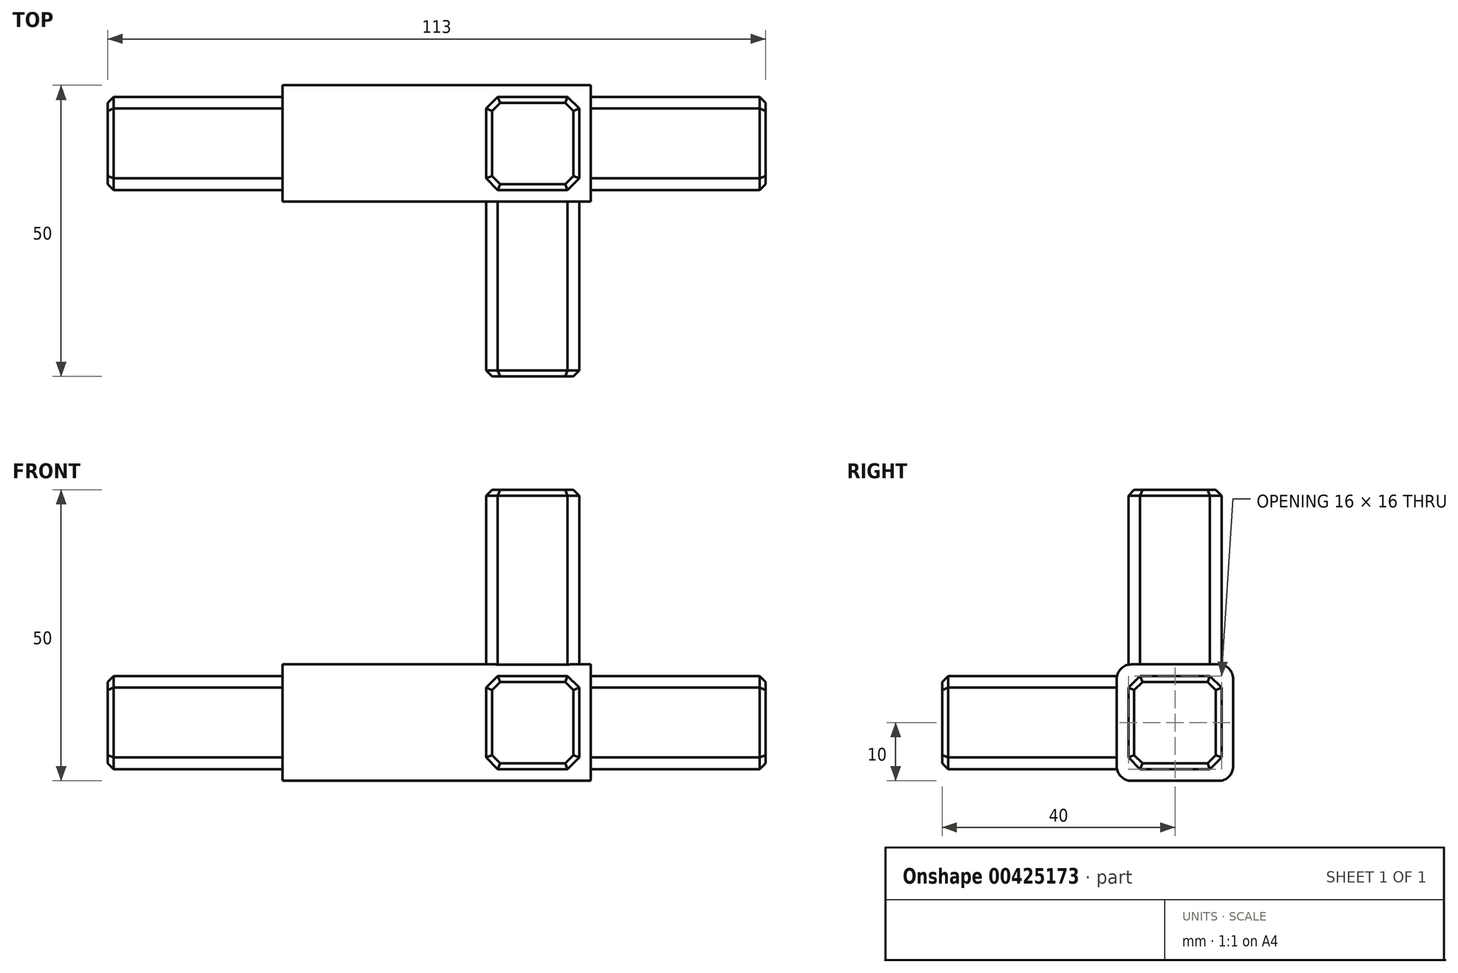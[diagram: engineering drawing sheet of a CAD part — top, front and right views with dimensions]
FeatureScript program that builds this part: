
annotation { "Feature Type Name" : "Feature", "Feature Type Description" : "" }
export const myFeature = defineFeature(function(context is Context, id is Id, definition is map)
    precondition{}
    {
        {
            var Q0;
            Q0=qCreatedBy(makeId("Front.planeOp"),FACE);
            var sketch = newSketch(context, id + "F0", { "sketchPlane" : qUnion([Q0])});
            skLineSegment(sketch, "E0.bottom", {"start": v(-10, -10) * mm, "end": v(10, -10) * mm});
            skLineSegment(sketch, "E0.top", {"start": v(-10, 10) * mm, "end": v(10, 10) * mm});
            skLineSegment(sketch, "E0.left", {"start": v(-10, -10) * mm, "end": v(-10, 10) * mm});
            skLineSegment(sketch, "E0.right", {"start": v(10, -10) * mm, "end": v(10, 10) * mm});
            skPoint(sketch, "E0.middle", {"position": v(0, 0) * mm});
            skLineSegment(sketch, "E1.bottom", {"start": v(-8, -8) * mm, "end": v(8, -8) * mm});
            skLineSegment(sketch, "E1.top", {"start": v(-8, 8) * mm, "end": v(8, 8) * mm});
            skLineSegment(sketch, "E1.left", {"start": v(-8, -8) * mm, "end": v(-8, 8) * mm});
            skLineSegment(sketch, "E1.right", {"start": v(8, -8) * mm, "end": v(8, 8) * mm});
            skSolve(sketch);
        }
        {
            var Q0;
            Q0=makeQuery(id+"F0.imprint","IMPRINT",FACE,{"disambiguationData":[TD([[makeQuery(id+"F0.imprint","IMPRINT",EDGE,{"derivedFrom":sQuery(id+"F0.wireOp",EDGE,"E1.bottom")}),1.0]])]});
            extrude(context, id + "F1", {"entities" : qUnion([Q0]), "depth" : 50 * mm});
        }
        {
            var Q0;
            Q0=qSketchRegion(id+"F0",true);
            extrude(context, id + "F2", {"entities" : qUnion([Q0]), "operationType" : NewBodyOperationType.ADD, "depth" : 20 * mm});
        }
        {
            var Q0;
            Q0=qCreatedBy(makeId("Right.planeOp"),FACE);
            var sketch = newSketch(context, id + "F3", { "sketchPlane" : qUnion([Q0])});
            skLineSegment(sketch, "E2.bottom", {"start": v(-2, -8) * mm, "end": v(-18, -8) * mm});
            skLineSegment(sketch, "E2.top", {"start": v(-2, 8) * mm, "end": v(-18, 8) * mm});
            skLineSegment(sketch, "E2.left", {"start": v(-2, -8) * mm, "end": v(-2, 8) * mm});
            skLineSegment(sketch, "E2.right", {"start": v(-18, -8) * mm, "end": v(-18, 8) * mm});
            skPoint(sketch, "E2.middle", {"position": v(-10, 0) * mm});
            skSolve(sketch);
        }
        {
            var Q0;
            Q0=qSketchRegion(id+"F3",true);
            extrude(context, id + "F4", {"entities" : qUnion([Q0]), "operationType" : NewBodyOperationType.ADD, "depth" : 40 * mm});
        }
        {
            var Q0;
            Q0=qCreatedBy(makeId("Right.planeOp"),FACE);
            var sketch = newSketch(context, id + "F5", { "sketchPlane" : qUnion([Q0])});
            skLineSegment(sketch, "E3.bottom", {"start": v(-2, -8) * mm, "end": v(-18, -8) * mm});
            skLineSegment(sketch, "E3.top", {"start": v(-2, 8) * mm, "end": v(-18, 8) * mm});
            skLineSegment(sketch, "E3.left", {"start": v(-2, -8) * mm, "end": v(-2, 8) * mm});
            skLineSegment(sketch, "E3.right", {"start": v(-18, -8) * mm, "end": v(-18, 8) * mm});
            skPoint(sketch, "E3.middle", {"position": v(-10, 0) * mm});
            skSolve(sketch);
        }
        {
            var Q0;
            Q0=qSketchRegion(id+"F5",true);
            extrude(context, id + "F6", {"entities" : qUnion([Q0]), "operationType" : NewBodyOperationType.ADD, "oppositeDirection" : true, "depth" : 73 * mm});
        }
        {
            var Q0;
            Q0=qCreatedBy(makeId("Top.planeOp"),FACE);
            var sketch = newSketch(context, id + "F7", { "sketchPlane" : qUnion([Q0])});
            skLineSegment(sketch, "E4.bottom", {"start": v(-8, -18) * mm, "end": v(8, -18) * mm});
            skLineSegment(sketch, "E4.top", {"start": v(-8, -2) * mm, "end": v(8, -2) * mm});
            skLineSegment(sketch, "E4.left", {"start": v(-8, -18) * mm, "end": v(-8, -2) * mm});
            skLineSegment(sketch, "E4.right", {"start": v(8, -18) * mm, "end": v(8, -2) * mm});
            skPoint(sketch, "E4.middle", {"position": v(0, -10) * mm});
            skSolve(sketch);
        }
        {
            var Q0;
            Q0=qSketchRegion(id+"F7",true);
            extrude(context, id + "F8", {"entities" : qUnion([Q0]), "operationType" : NewBodyOperationType.ADD, "depth" : 40 * mm});
        }
        {
            var Q0;
            Q0=makeQuery(id+"F2.opExtrude","SWEPT_FACE",FACE,{"disambiguationData":[OSD([sQuery(id+"F0.wireOp",EDGE,"E0.left")])]});
            extrude(context, id + "F9", {"entities" : qUnion([Q0]), "operationType" : NewBodyOperationType.ADD, "depth" : 33 * mm});
        }
        {
            var Q0;
            {var subQ0=sQuery(id+"F0.wireOp",EDGE,"E0.left");var subQ1=sQuery(id+"F0.wireOp",EDGE,"E0.top");Q0=makeQuery(id+"F9.boolean.opBoolean","MERGE",EDGE,{"derivedFrom":[makeQuery(id+"F2.opExtrude","CAP_EDGE",EDGE,{"disambiguationData":[OSD([subQ1])],"isStart":false}),makeQuery(id+"F9.opExtrude","SWEPT_EDGE",EDGE,{"disambiguationData":[OSD([subQ1,subQ0]),TDD([makeQuery(id+"F2.opExtrude","CAP_VERTEX",VERTEX,{"disambiguationData":[OSD([subQ1,subQ0])],"isStart":false})])]})]});}
            var Q1;
            {var subQ0=sQuery(id+"F0.wireOp",EDGE,"E0.left");var subQ1=sQuery(id+"F0.wireOp",EDGE,"E0.bottom");Q1=makeQuery(id+"F9.boolean.opBoolean","MERGE",EDGE,{"derivedFrom":[makeQuery(id+"F2.opExtrude","CAP_EDGE",EDGE,{"disambiguationData":[OSD([subQ1])],"isStart":false}),makeQuery(id+"F9.opExtrude","SWEPT_EDGE",EDGE,{"disambiguationData":[OSD([subQ1,subQ0]),TDD([makeQuery(id+"F2.opExtrude","CAP_VERTEX",VERTEX,{"disambiguationData":[OSD([subQ1,subQ0])],"isStart":false})])]})]});}
            var Q2;
            {var subQ0=sQuery(id+"F0.wireOp",EDGE,"E0.left");var subQ1=sQuery(id+"F0.wireOp",EDGE,"E0.top");Q2=makeQuery(id+"F9.boolean.opBoolean","MERGE",EDGE,{"derivedFrom":[makeQuery(id+"F2.opExtrude","CAP_EDGE",EDGE,{"disambiguationData":[OSD([subQ1])],"isStart":true}),makeQuery(id+"F9.opExtrude","SWEPT_EDGE",EDGE,{"disambiguationData":[OSD([subQ1,subQ0]),TDD([makeQuery(id+"F2.opExtrude","CAP_VERTEX",VERTEX,{"disambiguationData":[OSD([subQ1,subQ0])],"isStart":true})])]})]});}
            var Q3;
            {var subQ0=sQuery(id+"F0.wireOp",EDGE,"E0.left");var subQ1=sQuery(id+"F0.wireOp",EDGE,"E0.bottom");Q3=makeQuery(id+"F9.boolean.opBoolean","MERGE",EDGE,{"derivedFrom":[makeQuery(id+"F2.opExtrude","CAP_EDGE",EDGE,{"disambiguationData":[OSD([subQ1])],"isStart":true}),makeQuery(id+"F9.opExtrude","SWEPT_EDGE",EDGE,{"disambiguationData":[OSD([subQ1,subQ0]),TDD([makeQuery(id+"F2.opExtrude","CAP_VERTEX",VERTEX,{"disambiguationData":[OSD([subQ1,subQ0])],"isStart":true})])]})]});}
            fillet(context, id + "F10", {"entities" : qUnion([Q0, Q1, Q2, Q3]), "radius" : 2.5 * mm, "tangentPropagation" : true, "allowEdgeOverflow" : false});
        }
        {
            var Q0;
            Q0=makeQuery(id+"F6.opExtrude","SWEPT_EDGE",EDGE,{"disambiguationData":[OSD([sQuery(id+"F5.wireOp",EDGE,"E3.top"),sQuery(id+"F5.wireOp",EDGE,"E3.right")])]});
            var Q1;
            Q1=makeQuery(id+"F6.opExtrude","SWEPT_EDGE",EDGE,{"disambiguationData":[OSD([sQuery(id+"F5.wireOp",EDGE,"E3.bottom"),sQuery(id+"F5.wireOp",EDGE,"E3.right")])]});
            var Q2;
            Q2=makeQuery(id+"F6.opExtrude","SWEPT_EDGE",EDGE,{"disambiguationData":[OSD([sQuery(id+"F5.wireOp",EDGE,"E3.top"),sQuery(id+"F5.wireOp",EDGE,"E3.left")])]});
            var Q3;
            Q3=makeQuery(id+"F6.opExtrude","SWEPT_EDGE",EDGE,{"disambiguationData":[OSD([sQuery(id+"F5.wireOp",EDGE,"E3.bottom"),sQuery(id+"F5.wireOp",EDGE,"E3.left")])]});
            var Q4;
            Q4=makeQuery(id+"F1.opExtrude","SWEPT_EDGE",EDGE,{"disambiguationData":[OSD([sQuery(id+"F0.wireOp",EDGE,"E1.top"),sQuery(id+"F0.wireOp",EDGE,"E1.left")])]});
            var Q5;
            Q5=makeQuery(id+"F1.opExtrude","SWEPT_EDGE",EDGE,{"disambiguationData":[OSD([sQuery(id+"F0.wireOp",EDGE,"E1.bottom"),sQuery(id+"F0.wireOp",EDGE,"E1.left")])]});
            var Q6;
            Q6=makeQuery(id+"F1.opExtrude","SWEPT_EDGE",EDGE,{"disambiguationData":[OSD([sQuery(id+"F0.wireOp",EDGE,"E1.top"),sQuery(id+"F0.wireOp",EDGE,"E1.right")])]});
            var Q7;
            Q7=makeQuery(id+"F1.opExtrude","SWEPT_EDGE",EDGE,{"disambiguationData":[OSD([sQuery(id+"F0.wireOp",EDGE,"E1.bottom"),sQuery(id+"F0.wireOp",EDGE,"E1.right")])]});
            var Q8;
            Q8=makeQuery(id+"F4.opExtrude","SWEPT_EDGE",EDGE,{"disambiguationData":[OSD([sQuery(id+"F3.wireOp",EDGE,"E2.bottom"),sQuery(id+"F3.wireOp",EDGE,"E2.right")])]});
            var Q9;
            Q9=makeQuery(id+"F4.opExtrude","SWEPT_EDGE",EDGE,{"disambiguationData":[OSD([sQuery(id+"F3.wireOp",EDGE,"E2.top"),sQuery(id+"F3.wireOp",EDGE,"E2.right")])]});
            var Q10;
            Q10=makeQuery(id+"F8.opExtrude","SWEPT_EDGE",EDGE,{"disambiguationData":[OSD([sQuery(id+"F7.wireOp",EDGE,"E4.bottom"),sQuery(id+"F7.wireOp",EDGE,"E4.right")])]});
            var Q11;
            Q11=makeQuery(id+"F8.opExtrude","SWEPT_EDGE",EDGE,{"disambiguationData":[OSD([sQuery(id+"F7.wireOp",EDGE,"E4.bottom"),sQuery(id+"F7.wireOp",EDGE,"E4.left")])]});
            var Q12;
            Q12=makeQuery(id+"F4.opExtrude","SWEPT_EDGE",EDGE,{"disambiguationData":[OSD([sQuery(id+"F3.wireOp",EDGE,"E2.bottom"),sQuery(id+"F3.wireOp",EDGE,"E2.left")])]});
            var Q13;
            Q13=makeQuery(id+"F4.opExtrude","SWEPT_EDGE",EDGE,{"disambiguationData":[OSD([sQuery(id+"F3.wireOp",EDGE,"E2.top"),sQuery(id+"F3.wireOp",EDGE,"E2.left")])]});
            var Q14;
            Q14=makeQuery(id+"F8.opExtrude","SWEPT_EDGE",EDGE,{"disambiguationData":[OSD([sQuery(id+"F7.wireOp",EDGE,"E4.top"),sQuery(id+"F7.wireOp",EDGE,"E4.right")])]});
            var Q15;
            Q15=makeQuery(id+"F8.opExtrude","SWEPT_EDGE",EDGE,{"disambiguationData":[OSD([sQuery(id+"F7.wireOp",EDGE,"E4.top"),sQuery(id+"F7.wireOp",EDGE,"E4.left")])]});
            chamfer(context, id + "F11", {"entities" : qUnion([Q0, Q1, Q2, Q3, Q4, Q5, Q6, Q7, Q8, Q9, Q10, Q11, Q12, Q13, Q14, Q15]), "width" : 2 * mm, "tangentPropagation" : true});
        }
        {
            var Q0;
            Q0=makeQuery(id+"F6.opExtrude","CAP_EDGE",EDGE,{"disambiguationData":[OSD([sQuery(id+"F5.wireOp",EDGE,"E3.top")])],"isStart":false});
            var Q1;
            Q1=makeQuery(id+"F6.opExtrude","CAP_FACE",FACE,{"disambiguationData":[OSD([sQuery(id+"F5.wireOp",EDGE,"E3.bottom"),sQuery(id+"F5.wireOp",EDGE,"E3.top"),sQuery(id+"F5.wireOp",EDGE,"E3.left"),sQuery(id+"F5.wireOp",EDGE,"E3.right")])],"isStart":false});
            var Q2;
            Q2=makeQuery(id+"F1.opExtrude","CAP_FACE",FACE,{"disambiguationData":[OSD([sQuery(id+"F0.wireOp",EDGE,"E1.bottom"),sQuery(id+"F0.wireOp",EDGE,"E1.top"),sQuery(id+"F0.wireOp",EDGE,"E1.left"),sQuery(id+"F0.wireOp",EDGE,"E1.right")])],"isStart":false});
            var Q3;
            Q3=makeQuery(id+"F8.opExtrude","CAP_FACE",FACE,{"disambiguationData":[OSD([sQuery(id+"F7.wireOp",EDGE,"E4.bottom"),sQuery(id+"F7.wireOp",EDGE,"E4.top"),sQuery(id+"F7.wireOp",EDGE,"E4.left"),sQuery(id+"F7.wireOp",EDGE,"E4.right")])],"isStart":false});
            var Q4;
            Q4=makeQuery(id+"F4.opExtrude","CAP_FACE",FACE,{"disambiguationData":[OSD([sQuery(id+"F3.wireOp",EDGE,"E2.bottom"),sQuery(id+"F3.wireOp",EDGE,"E2.top"),sQuery(id+"F3.wireOp",EDGE,"E2.left"),sQuery(id+"F3.wireOp",EDGE,"E2.right")])],"isStart":false});
            chamfer(context, id + "F12", {"entities" : qUnion([Q0, Q1, Q2, Q3, Q4]), "width" : 1 * mm, "tangentPropagation" : true});
        }
    });
